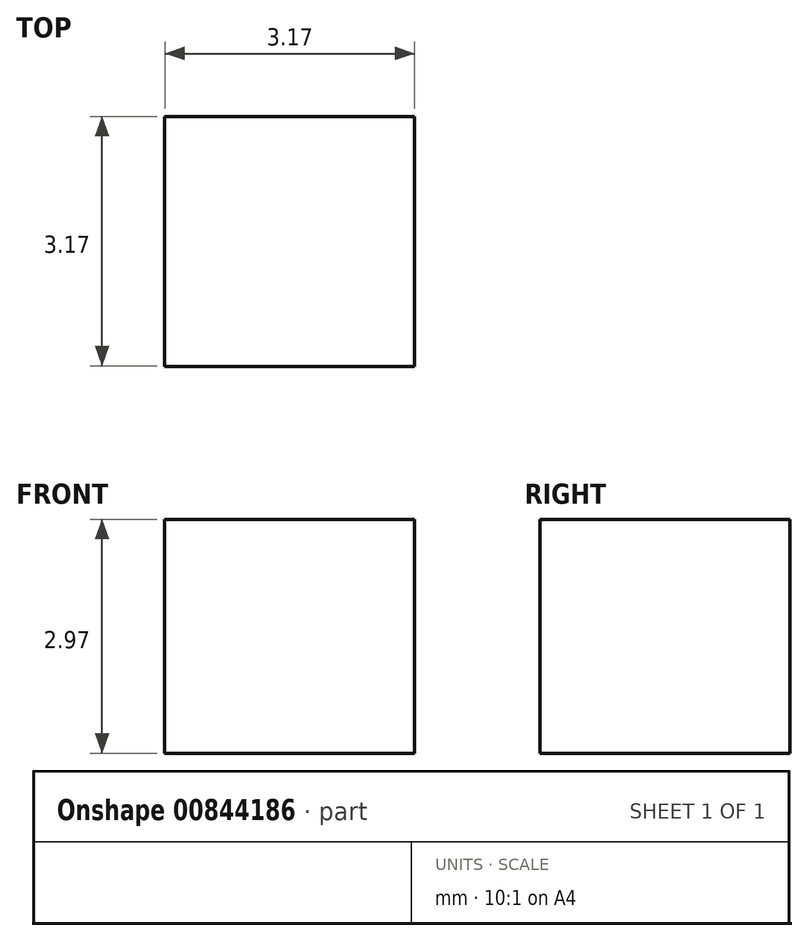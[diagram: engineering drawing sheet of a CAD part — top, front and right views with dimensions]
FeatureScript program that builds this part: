
annotation { "Feature Type Name" : "Feature", "Feature Type Description" : "" }
export const myFeature = defineFeature(function(context is Context, id is Id, definition is map)
    precondition{}
    {
        {
            var Q0;
            Q0=qCreatedBy(makeId("Front.planeOp"),FACE);
            var sketch = newSketch(context, id + "F0", { "sketchPlane" : qUnion([Q0])});
            skArc(sketch, "E0", {"start": v(63.5, 0) * mm, "mid": v(0, 63.5) * mm, "end": v(-63.5, 0) * mm});
            skArc(sketch, "E1", {"start": v(53.98, 0) * mm, "mid": v(0, 53.98) * mm, "end": v(-53.98, 0) * mm});
            skPoint(sketch, "E2.orphan", {"position": v(-73.05, 0) * mm});
            skLineSegment(sketch, "E3.trimOffspring", {"start": v(53.98, 0) * mm, "end": v(63.5, 0) * mm});
            skLineSegment(sketch, "E4", {"start": v(-60.83, 18.23) * mm, "end": v(-56.34, 16.72) * mm});
            skLineSegment(sketch, "E5", {"start": v(-56.34, 16.72) * mm, "end": v(-55.4, 19.5) * mm});
            skLineSegment(sketch, "E6", {"start": v(-55.4, 19.5) * mm, "end": v(-59.93, 21) * mm});
            skLineSegment(sketch, "E7.6.0", {"start": v(59.92, 21) * mm, "end": v(55.4, 19.59) * mm});
            skLineSegment(sketch, "E7.6.1", {"start": v(55.4, 19.59) * mm, "end": v(56.28, 16.8) * mm});
            skLineSegment(sketch, "E7.6.2", {"start": v(56.28, 16.8) * mm, "end": v(60.83, 18.23) * mm});
            skLineSegment(sketch, "E7.7.0", {"start": v(36.13, 52.22) * mm, "end": v(33.31, 48.41) * mm});
            skLineSegment(sketch, "E7.7.1", {"start": v(33.31, 48.41) * mm, "end": v(35.66, 46.67) * mm});
            skLineSegment(sketch, "E7.7.2", {"start": v(35.66, 46.67) * mm, "end": v(38.5, 50.5) * mm});
            skLineSegment(sketch, "E7.8.0", {"start": v(-1.46, 63.48) * mm, "end": v(-1.5, 58.75) * mm});
            skLineSegment(sketch, "E7.8.1", {"start": v(-1.5, 58.75) * mm, "end": v(1.42, 58.72) * mm});
            skLineSegment(sketch, "E7.8.2", {"start": v(1.42, 58.72) * mm, "end": v(1.46, 63.48) * mm});
            skLineSegment(sketch, "E7.9.0", {"start": v(-38.5, 50.5) * mm, "end": v(-35.75, 46.64) * mm});
            skLineSegment(sketch, "E7.9.1", {"start": v(-35.75, 46.64) * mm, "end": v(-33.37, 48.34) * mm});
            skLineSegment(sketch, "E7.9.2", {"start": v(-33.37, 48.34) * mm, "end": v(-36.14, 52.22) * mm});
            skLineSegment(sketch, "E8.top", {"start": v(-57.15, 0) * mm, "end": v(-53.52, 0) * mm});
            skLineSegment(sketch, "E8.left", {"start": v(-57.15, 2.97) * mm, "end": v(-57.15, 0) * mm});
            skLineSegment(sketch, "E9", {"start": v(-57.15, 2.97) * mm, "end": v(-53.56, 2.97) * mm});
            skLineSegment(sketch, "E10.bottom", {"start": v(53.98, 0) * mm, "end": v(57.15, 0) * mm});
            skLineSegment(sketch, "E10.top", {"start": v(53.98, 2.97) * mm, "end": v(57.15, 2.97) * mm});
            skLineSegment(sketch, "E10.left", {"start": v(53.98, 0) * mm, "end": v(53.98, 2.97) * mm});
            skLineSegment(sketch, "E10.right", {"start": v(57.15, 0) * mm, "end": v(57.15, 2.97) * mm});
            skLineSegment(sketch, "E11", {"start": v(53.98, 2.97) * mm, "end": v(53.16, 2.97) * mm});
            skLineSegment(sketch, "E12", {"start": v(-63.5, 0) * mm, "end": v(-57.15, 0) * mm});
            skSolve(sketch);
        }
        {
            var Q0;
            {var subQ11=sQuery(id+"F0.wireOp",EDGE,"E3.trimOffspring");Q0=makeQuery(id+"F0.imprint","IMPRINT",FACE,{"disambiguationData":[TD([[makeQuery(id+"F0.imprint","IMPRINT",EDGE,{"derivedFrom":subQ11}),1.0]])]});}
            extrude(context, id + "F1", {"entities" : qUnion([Q0]), "depth" : 3.17 * mm, "offsetDistance" : 25.4 * mm});
        }
    });
